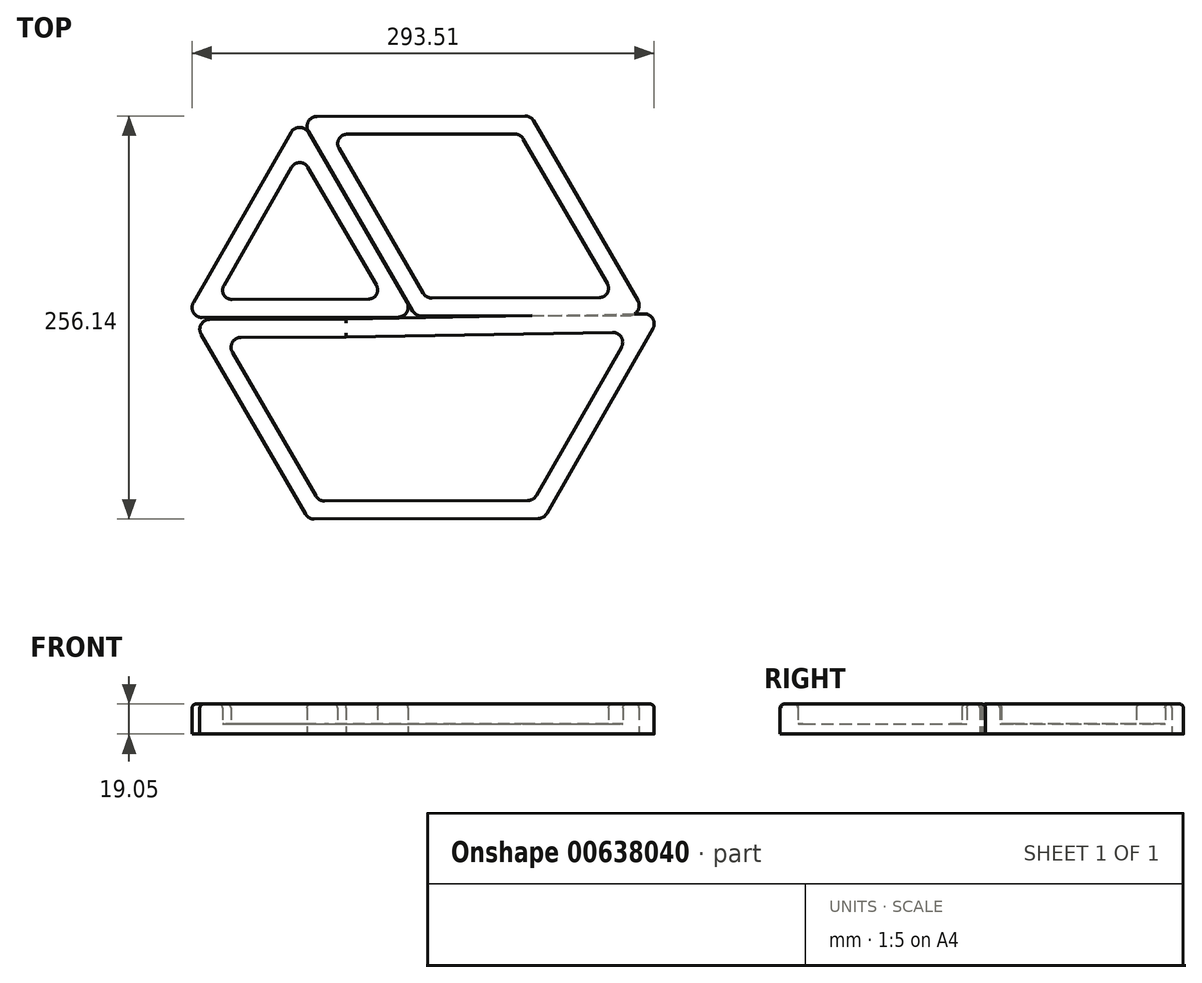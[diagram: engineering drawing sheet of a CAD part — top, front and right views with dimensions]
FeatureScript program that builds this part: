
annotation { "Feature Type Name" : "Feature", "Feature Type Description" : "" }
export const myFeature = defineFeature(function(context is Context, id is Id, definition is map)
    precondition{}
    {
        {
            var Q0;
            Q0=qCreatedBy(makeId("Top.planeOp"),FACE);
            var sketch = newSketch(context, id + "F0", { "sketchPlane" : qUnion([Q0])});
            skLineSegment(sketch, "E0.1", {"start": v(156.04, 3.36) * mm, "end": v(81.33, -126.86) * mm, "construction": true});
            skLineSegment(sketch, "E0.2", {"start": v(81.33, -126.86) * mm, "end": v(-68.24, -127.26) * mm, "construction": true});
            skLineSegment(sketch, "E0.3", {"start": v(-68.24, -127.26) * mm, "end": v(-141.91, -0.46) * mm, "construction": true});
            skLineSegment(sketch, "E1", {"start": v(-130.91, -0.43) * mm, "end": v(-44.37, -0.2) * mm});
            skLineSegment(sketch, "E2", {"start": v(-44.54, -0.2) * mm, "end": v(144.85, 3.16) * mm});
            skLineSegment(sketch, "E3", {"start": v(83.16, -123.68) * mm, "end": v(150.47, -6.35) * mm});
            skLineSegment(sketch, "E4", {"start": v(77.67, -126.87) * mm, "end": v(-64.58, -127.25) * mm});
            skLineSegment(sketch, "E5", {"start": v(-70.09, -124.1) * mm, "end": v(-136.39, -9.97) * mm});
            skLineSegment(sketch, "E6.0", {"start": v(-44.34, -11.63) * mm, "end": v(124.91, -8.63) * mm});
            skLineSegment(sketch, "E6.1", {"start": v(76.53, -112.26) * mm, "end": v(130.53, -18.14) * mm});
            skLineSegment(sketch, "E6.2", {"start": v(-111.08, -11.8) * mm, "end": v(-44.34, -11.63) * mm});
            skLineSegment(sketch, "E6.3", {"start": v(-63.52, -112.64) * mm, "end": v(-116.56, -21.35) * mm});
            skLineSegment(sketch, "E6.4", {"start": v(71.04, -115.45) * mm, "end": v(-58.01, -115.8) * mm});
            skPoint(sketch, "E7.visualSharp", {"position": v(-122.08, -11.84) * mm});
            skArc(sketch, "E7.filletArc", {"start": v(-111.08, -11.8) * mm, "mid": v(-116.58, -15) * mm, "end": v(-116.56, -21.35) * mm});
            skPoint(sketch, "E8.visualSharp", {"position": v(-61.68, -115.81) * mm});
            skArc(sketch, "E8.filletArc", {"start": v(-63.52, -112.64) * mm, "mid": v(-61.19, -114.96) * mm, "end": v(-58.01, -115.8) * mm});
            skPoint(sketch, "E9.visualSharp", {"position": v(74.7, -115.44) * mm});
            skArc(sketch, "E9.filletArc", {"start": v(71.04, -115.45) * mm, "mid": v(74.21, -114.6) * mm, "end": v(76.53, -112.26) * mm});
            skPoint(sketch, "E10.visualSharp", {"position": v(136.1, -8.43) * mm});
            skArc(sketch, "E10.filletArc", {"start": v(130.53, -18.14) * mm, "mid": v(130.5, -11.75) * mm, "end": v(124.91, -8.63) * mm});
            skPoint(sketch, "E11.visualSharp", {"position": v(-68.24, -127.26) * mm});
            skArc(sketch, "E11.filletArc", {"start": v(-70.09, -124.1) * mm, "mid": v(-67.76, -126.4) * mm, "end": v(-64.58, -127.25) * mm});
            skPoint(sketch, "E12.visualSharp", {"position": v(81.33, -126.86) * mm});
            skArc(sketch, "E12.filletArc", {"start": v(77.67, -126.87) * mm, "mid": v(80.84, -126) * mm, "end": v(83.16, -123.68) * mm});
            skPoint(sketch, "E13.visualSharp", {"position": v(-141.91, -0.46) * mm});
            skArc(sketch, "E13.filletArc", {"start": v(-130.91, -0.43) * mm, "mid": v(-136.4, -3.62) * mm, "end": v(-136.39, -9.97) * mm});
            skPoint(sketch, "E14.visualSharp", {"position": v(156.04, 3.36) * mm});
            skArc(sketch, "E14.filletArc", {"start": v(150.47, -6.35) * mm, "mid": v(150.43, 0.04) * mm, "end": v(144.85, 3.16) * mm});
            skSolve(sketch);
        }
        {
            var Q0;
            Q0=qCreatedBy(makeId("Top.planeOp"),FACE);
            var sketch = newSketch(context, id + "F1", { "sketchPlane" : qUnion([Q0])});
            skLineSegment(sketch, "E15.0", {"start": v(72.83, 128.9) * mm, "end": v(146.5, 2.1) * mm, "construction": true});
            skLineSegment(sketch, "E15.5", {"start": v(-160.44, 128.26) * mm, "end": v(72.83, 128.9) * mm, "construction": true});
            skLineSegment(sketch, "E16", {"start": v(-68.3, 118.99) * mm, "end": v(-2, 4.87) * mm});
            skLineSegment(sketch, "E17", {"start": v(3.52, 1.7) * mm, "end": v(135.5, 2.07) * mm});
            skLineSegment(sketch, "E18", {"start": v(-62.82, 128.53) * mm, "end": v(69.16, 128.89) * mm});
            skLineSegment(sketch, "E19", {"start": v(140.97, 11.6) * mm, "end": v(74.67, 125.73) * mm});
            skLineSegment(sketch, "E20.0", {"start": v(-43.82, 117.15) * mm, "end": v(62.6, 117.44) * mm});
            skLineSegment(sketch, "E20.1", {"start": v(-48.88, 108.33) * mm, "end": v(4.58, 16.32) * mm});
            skLineSegment(sketch, "E20.2", {"start": v(10.08, 13.16) * mm, "end": v(116.5, 13.44) * mm});
            skLineSegment(sketch, "E20.3", {"start": v(121.56, 22.27) * mm, "end": v(68.1, 114.28) * mm});
            skArc(sketch, "E21.filletArc", {"start": v(-43.82, 117.15) * mm, "mid": v(-48.9, 114.2) * mm, "end": v(-48.88, 108.33) * mm});
            skArc(sketch, "E22.filletArc", {"start": v(4.58, 16.32) * mm, "mid": v(6.9, 14) * mm, "end": v(10.08, 13.16) * mm});
            skArc(sketch, "E23.filletArc", {"start": v(116.5, 13.44) * mm, "mid": v(121.57, 16.4) * mm, "end": v(121.56, 22.27) * mm});
            skArc(sketch, "E24.filletArc", {"start": v(68.1, 114.28) * mm, "mid": v(65.77, 116.6) * mm, "end": v(62.6, 117.44) * mm});
            skPoint(sketch, "E25.visualSharp", {"position": v(-73.82, 128.5) * mm});
            skArc(sketch, "E25.filletArc", {"start": v(-62.82, 128.53) * mm, "mid": v(-68.3, 125.34) * mm, "end": v(-68.3, 118.99) * mm});
            skPoint(sketch, "E26.visualSharp", {"position": v(72.83, 128.9) * mm});
            skArc(sketch, "E26.filletArc", {"start": v(74.67, 125.73) * mm, "mid": v(72.34, 128.04) * mm, "end": v(69.16, 128.89) * mm});
            skPoint(sketch, "E27.visualSharp", {"position": v(146.5, 2.1) * mm});
            skArc(sketch, "E27.filletArc", {"start": v(135.5, 2.07) * mm, "mid": v(140.99, 5.26) * mm, "end": v(140.97, 11.6) * mm});
            skPoint(sketch, "E28.visualSharp", {"position": v(-0.15, 1.7) * mm});
            skArc(sketch, "E28.filletArc", {"start": v(-2, 4.87) * mm, "mid": v(0.34, 2.55) * mm, "end": v(3.52, 1.7) * mm});
            skSolve(sketch);
        }
        {
            var Q0;
            Q0=qCreatedBy(makeId("Top.planeOp"),FACE);
            var sketch = newSketch(context, id + "F2", { "sketchPlane" : qUnion([Q0])});
            skLineSegment(sketch, "E29.4", {"start": v(-146.82, 0.73) * mm, "end": v(-73.85, 127.93) * mm, "construction": true});
            skLineSegment(sketch, "E30", {"start": v(-135.83, 0.76) * mm, "end": v(-11.18, 1.1) * mm});
            skLineSegment(sketch, "E31", {"start": v(-68.32, 118.42) * mm, "end": v(-5.7, 10.64) * mm});
            skLineSegment(sketch, "E32", {"start": v(-79.32, 118.4) * mm, "end": v(-141.35, 10.27) * mm});
            skLineSegment(sketch, "E33.0", {"start": v(-78.85, 96.25) * mm, "end": v(-122, 21.04) * mm});
            skLineSegment(sketch, "E33.1", {"start": v(-68.67, 96.28) * mm, "end": v(-25.12, 21.3) * mm});
            skLineSegment(sketch, "E33.2", {"start": v(-116.88, 12.25) * mm, "end": v(-30.18, 12.48) * mm});
            skArc(sketch, "E34.filletArc", {"start": v(-122, 21.04) * mm, "mid": v(-121.98, 15.17) * mm, "end": v(-116.88, 12.25) * mm});
            skArc(sketch, "E35.filletArc", {"start": v(-68.67, 96.28) * mm, "mid": v(-73.77, 99.2) * mm, "end": v(-78.85, 96.25) * mm});
            skArc(sketch, "E36.filletArc", {"start": v(-30.18, 12.48) * mm, "mid": v(-25.1, 15.43) * mm, "end": v(-25.12, 21.3) * mm});
            skPoint(sketch, "E37.visualSharp", {"position": v(-73.85, 127.93) * mm});
            skArc(sketch, "E37.filletArc", {"start": v(-68.32, 118.42) * mm, "mid": v(-73.83, 121.58) * mm, "end": v(-79.32, 118.4) * mm});
            skPoint(sketch, "E38.visualSharp", {"position": v(-0.18, 1.13) * mm});
            skArc(sketch, "E38.filletArc", {"start": v(-11.18, 1.1) * mm, "mid": v(-5.69, 4.3) * mm, "end": v(-5.7, 10.64) * mm});
            skPoint(sketch, "E39.visualSharp", {"position": v(-146.82, 0.73) * mm});
            skArc(sketch, "E39.filletArc", {"start": v(-141.35, 10.27) * mm, "mid": v(-141.33, 3.92) * mm, "end": v(-135.83, 0.76) * mm});
            skSolve(sketch);
        }
        {
            var Q0;
            Q0=makeQuery(id+"F0.imprint","IMPRINT",FACE,{"disambiguationData":[TD([[makeQuery(id+"F0.imprint","IMPRINT",EDGE,{"derivedFrom":sQuery(id+"F0.wireOp",EDGE,"E1")}),-1.0]])]});
            extrude(context, id + "F3", {"entities" : qUnion([Q0]), "depth" : 19.05 * mm, "offsetDistance" : 25.4 * mm});
        }
        {
            var Q0;
            Q0=makeQuery(id+"F0.imprint","IMPRINT",FACE,{"disambiguationData":[TD([[makeQuery(id+"F0.imprint","IMPRINT",EDGE,{"derivedFrom":sQuery(id+"F0.wireOp",EDGE,"E6.0")}),-1.0]])]});
            extrude(context, id + "F4", {"entities" : qUnion([Q0]), "operationType" : NewBodyOperationType.ADD, "depth" : 6.35 * mm, "offsetDistance" : 25.4 * mm});
        }
        {
            var Q0;
            Q0=makeQuery(id+"F3.opExtrude","CAP_EDGE",EDGE,{"disambiguationData":[OSD([sQuery(id+"F0.wireOp",EDGE,"E6.0"),sQuery(id+"F0.wireOp",EDGE,"E6.2")])],"isStart":false});
            var Q1;
            Q1=makeQuery(id+"F3.opExtrude","CAP_EDGE",EDGE,{"disambiguationData":[OSD([sQuery(id+"F0.wireOp",EDGE,"E7.filletArc")])],"isStart":false});
            fillet(context, id + "F5", {"entities" : qUnion([Q0, Q1]), "radius" : 2.54 * mm, "tangentPropagation" : true, "allowEdgeOverflow" : false});
        }
        {
            var Q0;
            Q0=makeQuery(id+"F3.opExtrude","CAP_EDGE",EDGE,{"disambiguationData":[OSD([sQuery(id+"F0.wireOp",EDGE,"E1"),sQuery(id+"F0.wireOp",EDGE,"E2")])],"isStart":false});
            fillet(context, id + "F6", {"entities" : qUnion([Q0]), "radius" : 2.54 * mm, "tangentPropagation" : true, "allowEdgeOverflow" : false});
        }
        {
            var Q0;
            Q0=makeQuery(id+"F1.imprint","IMPRINT",FACE,{"disambiguationData":[TD([[makeQuery(id+"F1.imprint","IMPRINT",EDGE,{"derivedFrom":sQuery(id+"F1.wireOp",EDGE,"E16")}),1.0]])]});
            extrude(context, id + "F7", {"entities" : qUnion([Q0]), "depth" : 19.05 * mm, "offsetDistance" : 25.4 * mm});
        }
        {
            var Q0;
            Q0=makeQuery(id+"F1.imprint","IMPRINT",FACE,{"disambiguationData":[TD([[makeQuery(id+"F1.imprint","IMPRINT",EDGE,{"derivedFrom":sQuery(id+"F1.wireOp",EDGE,"E20.0")}),-1.0]])]});
            extrude(context, id + "F8", {"entities" : qUnion([Q0]), "operationType" : NewBodyOperationType.ADD, "depth" : 6.35 * mm, "offsetDistance" : 25.4 * mm});
        }
        {
            var Q0;
            Q0=makeQuery(id+"F7.opExtrude","CAP_EDGE",EDGE,{"disambiguationData":[OSD([sQuery(id+"F1.wireOp",EDGE,"E20.1")])],"isStart":false});
            var Q1;
            Q1=makeQuery(id+"F7.opExtrude","CAP_EDGE",EDGE,{"disambiguationData":[OSD([sQuery(id+"F1.wireOp",EDGE,"E16")])],"isStart":false});
            fillet(context, id + "F9", {"entities" : qUnion([Q0, Q1]), "radius" : 2.54 * mm, "tangentPropagation" : true, "allowEdgeOverflow" : false});
        }
        {
            var Q0;
            Q0=makeQuery(id+"F2.imprint","IMPRINT",FACE,{"disambiguationData":[TD([[makeQuery(id+"F2.imprint","IMPRINT",EDGE,{"derivedFrom":sQuery(id+"F2.wireOp",EDGE,"E30")}),1.0]])]});
            extrude(context, id + "F10", {"entities" : qUnion([Q0]), "depth" : 19.05 * mm, "offsetDistance" : 25.4 * mm});
        }
        {
            var Q0;
            Q0=makeQuery(id+"F2.imprint","IMPRINT",FACE,{"disambiguationData":[TD([[makeQuery(id+"F2.imprint","IMPRINT",EDGE,{"derivedFrom":sQuery(id+"F2.wireOp",EDGE,"E33.0")}),1.0]])]});
            extrude(context, id + "F11", {"entities" : qUnion([Q0]), "operationType" : NewBodyOperationType.ADD, "depth" : 6.35 * mm, "offsetDistance" : 25.4 * mm});
        }
        {
            var Q0;
            Q0=makeQuery(id+"F10.opExtrude","CAP_EDGE",EDGE,{"disambiguationData":[OSD([sQuery(id+"F2.wireOp",EDGE,"E33.0")])],"isStart":false});
            fillet(context, id + "F12", {"entities" : qUnion([Q0]), "radius" : 2.54 * mm, "tangentPropagation" : true, "allowEdgeOverflow" : false});
        }
        {
            var Q0;
            Q0=makeQuery(id+"F10.opExtrude","CAP_EDGE",EDGE,{"disambiguationData":[OSD([sQuery(id+"F2.wireOp",EDGE,"E32")])],"isStart":false});
            fillet(context, id + "F13", {"entities" : qUnion([Q0]), "radius" : 2.54 * mm, "tangentPropagation" : true, "allowEdgeOverflow" : false});
        }
    });
